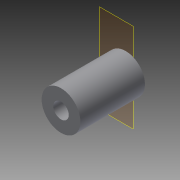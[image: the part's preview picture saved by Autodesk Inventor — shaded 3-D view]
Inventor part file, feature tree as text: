
AUTODESK INVENTOR PART (.ipt)
format: ipt  version: 2015 (Build 190159000, 159)  size: 75,776 bytes
history: native  units: in
note: dims shown in document units (in); Inventor stores cm internally (conversion verified against a paired STEP export)
features: plane x1, extrude x1, sketch x1, reference x1
ambient origin geometry x8: Origin, YZ Plane, XZ Plane, XY Plane, X Axis, Y Axis, Z Axis, Center Point
bodies: Solid1 (feature_tree)
feature tree (4):
  plane  "Work Plane1"
  extrude  "Extrusion1"  [1 undecoded]
  sketch  "Sketch1"  dims[d0=1.3226in d1=0.0in]
  reference  "Reference1"
note: 1 required parameter value undecoded (feature->parameter linkage not recoverable at this tier; creation-order binding heuristic only, values carry confidence <= 0.55)
